FREECAD ASSEMBLY — COMPONENT RECIPES ("Disco_assembly")

This assembly document has 6 components, labeled P0..P5 below (a component is one placed body or linked part). 0 of them carry a construction recipe — the FreeCAD feature program that regenerates the part from scratch, quoted from this document or its linked companion documents; the rest are supplied as boundary geometry only. No exploded tour is included for this assembly.
COMPONENT P0 — geometry summary ("Body"; no construction recipe available for this part):
  bounding box: 20.8 x 7.8 x 3.3 mm
  tessellated surface: 936 triangles
  volume: 253 mm^3 (47% of its bounding box)
  symmetry: mirror-symmetric across its y mid-plane
COMPONENT P1 — geometry summary ("Body001"; no construction recipe available for this part):
  bounding box: 20.8 x 7.8 x 3.3 mm
  tessellated surface: 936 triangles
  volume: 253 mm^3 (47% of its bounding box)
  symmetry: mirror-symmetric across its y mid-plane
COMPONENT P2 — geometry summary ("Body002"; no construction recipe available for this part):
  bounding box: 37.4 x 26.0 x 12.0 mm
  tessellated surface: 1,528 triangles
  volume: 1364 mm^3 (12% of its bounding box)
  symmetry: mirror-symmetric across its x mid-plane
COMPONENT P3 — geometry summary ("Body003"; no construction recipe available for this part):
  bounding box: 6.0 x 6.0 x 3.5 mm
  tessellated surface: 11,196 triangles
  volume: 73 mm^3 (58% of its bounding box)
  symmetry: mirror-symmetric across its x mid-plane
COMPONENT P4 — geometry summary ("Body004"; no construction recipe available for this part):
  bounding box: 34.0 x 34.0 x 31.7 mm
  tessellated surface: 40,532 triangles
  volume: 2831 mm^3 (8% of its bounding box)
  symmetry: 4-fold rotationally symmetric about the z axis; mirror-symmetric across its x mid-plane, y mid-plane
COMPONENT P5 — geometry summary ("ColorLEDdeck"; no construction recipe available for this part):
  bounding box: 32.4 x 32.4 x 0.8 mm
  tessellated surface: 1,396 triangles
  volume: 685 mm^3 (82% of its bounding box)
  symmetry: 2-fold rotationally symmetric about the x axis; 2-fold rotationally symmetric about the y axis; 2-fold rotationally symmetric about the z axis; mirror-symmetric across its x mid-plane, y mid-plane
PROVENANCE & LICENSES
A FreeCAD (.FCStd) document from a public repository crawl; recipes are the document's own serialized feature recipes (and, for linked parts, companion documents' recipes).
License: as declared in the source repository (recorded in the dataset sidecar).
